# Revit family: Digital_Media-Honeywell-Amplifier-580248(49)-11
name_source: partatom
category: Electrical Equipment
revit_build: Autodesk Revit 2017 (Build: 20160225_1515(x64)
units: mm (PartAtom-declared; Revit-internal decimal feet)

## family parameters
Cut with Voids When Loaded = No
Host = Face
OmniClass Number = 23.85.50.00
OmniClass Title = Communication Systems
Part Type = Equipment Switch
Room Calculation Point = No
Round Connector Dimension = Use Diameter
Shared = No

## types (2) — shared parameters
Air Humidity = 40 ... 93 %
Ambient Temperature = -5 °C ... 55 °C
Apparent Load = 0 VA
Default Elevation = 1219 mm
Depth = 400 mm
Finish = Metal - Honeywell - Stainless Steel - Black
Frequency = 50 Hz
Height = 68 mm
Load Sub-Classification = No
Manufacturer = Honeywell International
Manufacturer Fax Number = 02131/40615-606
Number of Poles = 1
Power Factor = 1
Product Documentation Link = https://www.esser-systems.com
Product Name = Four Channel Amplifier
Product Page URL = https://www.esser-systems.com
Rated Frequency = 50 ... 60 Hz (+10 % / -5 %)
Rated Load Current = 3 A
Rated Voltage = 230 V AC
Storage Temperature = -10 °C ... 55 °C
URL = www.esser-systems.com
Utility = No
Version = 2017 - v1.0a
Voltage = 230 V
Width = 484 mm

## per-type parameters (varying)
| type | Constraints | Description | Model | Power Output | Wattage | Watts | Weight |
| Four Channel amplifier 4XD300 - 580248.11 | 1 | Four channel amplifier 4XD300 | 580248.11 | 4 x 300 W | 300 W | 300 W | 13.80 kgf |
| Four Channel amplifier 4XD500 - 580249.11 | 2 | Four channel amplifier 4XD500 | 580249.11 | 4 x 500 W | 500 W | 500 W | 14.00 kgf |

## geometry (parser evidence)
native form markers: Sweep x3
no freeform markers — native parametric forms only
